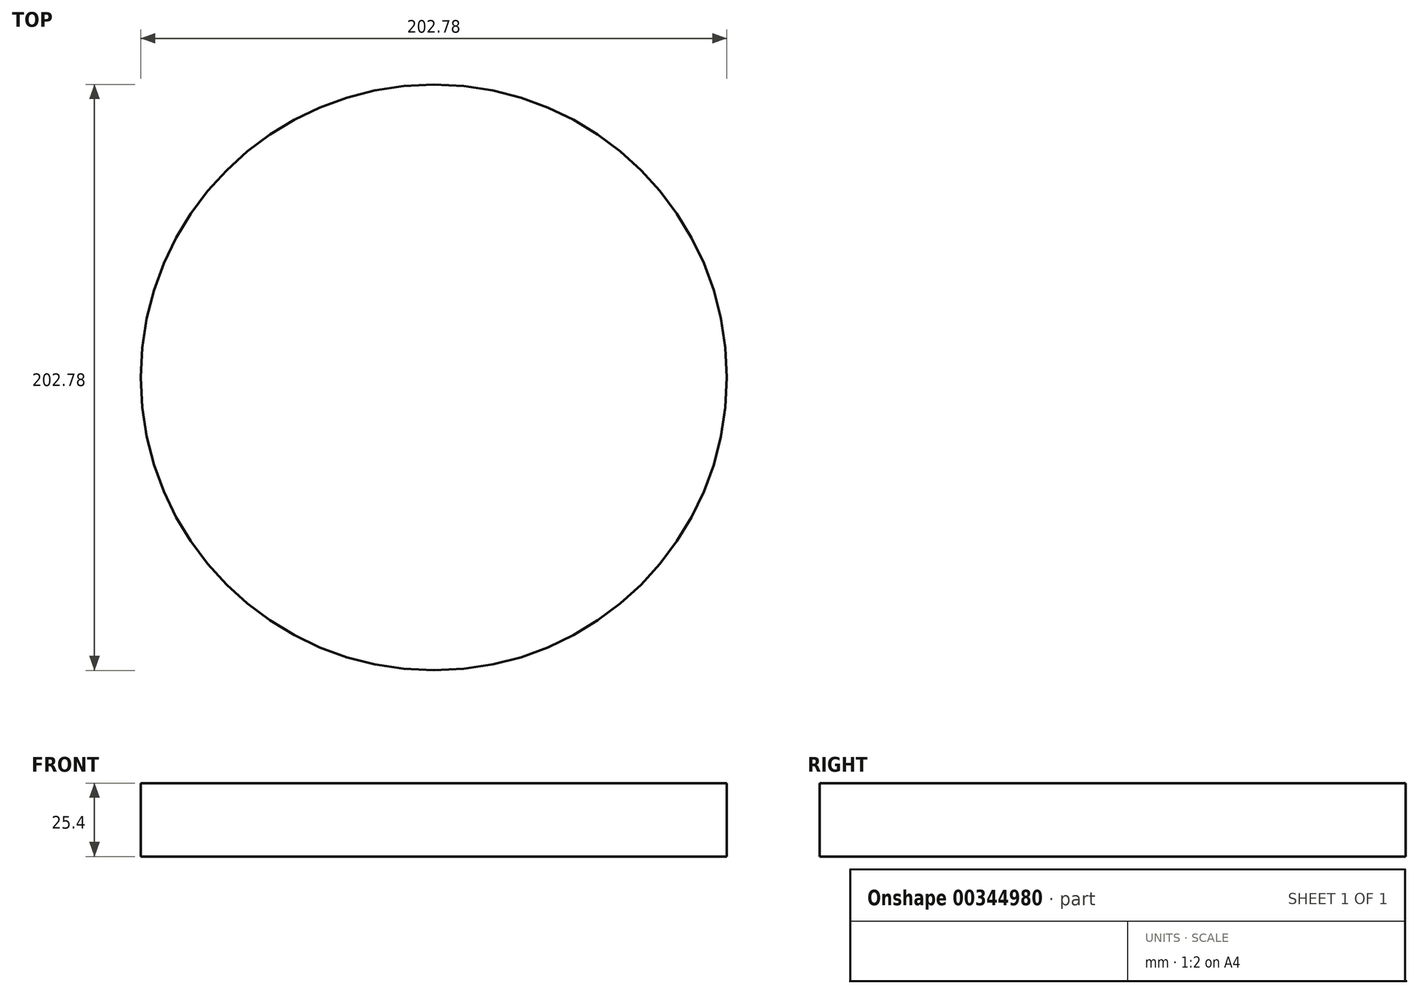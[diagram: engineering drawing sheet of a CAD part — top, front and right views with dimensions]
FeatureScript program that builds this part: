
annotation { "Feature Type Name" : "Feature", "Feature Type Description" : "" }
export const myFeature = defineFeature(function(context is Context, id is Id, definition is map)
    precondition{}
    {
        {
            var Q0;
            Q0=qCreatedBy(makeId("Top.planeOp"),FACE);
            var sketch = newSketch(context, id + "F0", { "sketchPlane" : qUnion([Q0])});
            skCircle(sketch, "E0", {"center": v(0, 0) * mm, "radius": 101.39 * mm});
            skSolve(sketch);
        }
        {
            var Q0;
            Q0=makeQuery(id+"F0.imprint","IMPRINT",FACE,{"disambiguationData":[TD([[makeQuery(id+"F0.imprint","IMPRINT",EDGE,{"derivedFrom":sQuery(id+"F0.wireOp",EDGE,"E0")}),1.0]])]});
            extrude(context, id + "F1", {"entities" : qUnion([Q0]), "depth" : 25.4 * mm});
        }
    });
